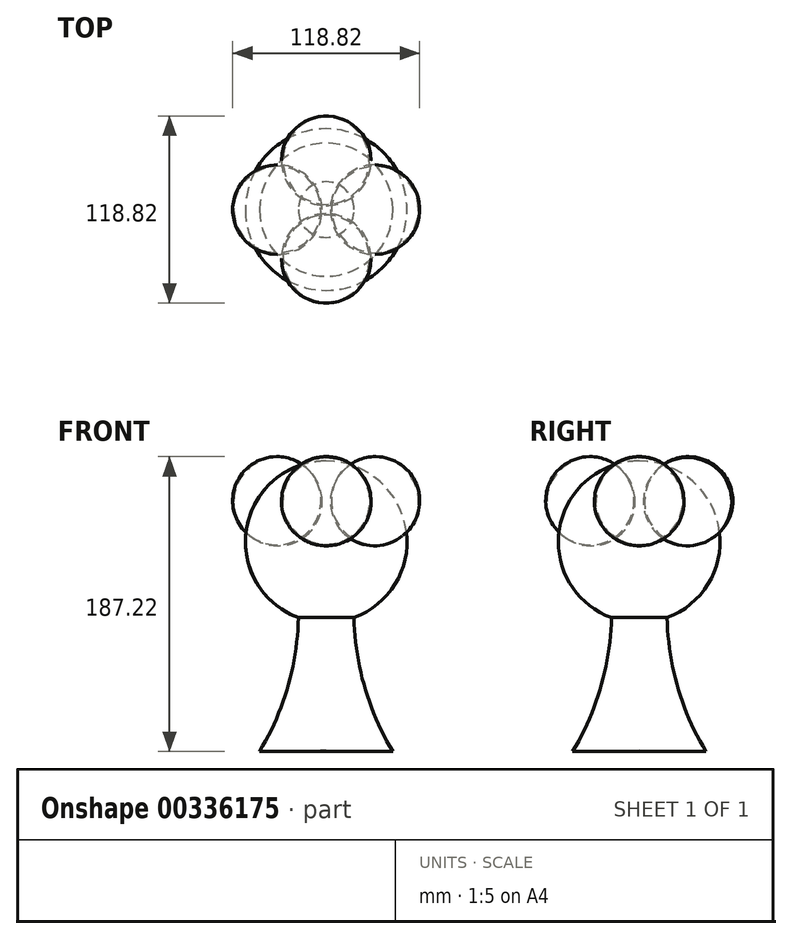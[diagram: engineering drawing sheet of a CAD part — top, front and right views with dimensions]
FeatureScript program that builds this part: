
annotation { "Feature Type Name" : "Feature", "Feature Type Description" : "" }
export const myFeature = defineFeature(function(context is Context, id is Id, definition is map)
    precondition{}
    {
        {
            var Q0;
            Q0=qCreatedBy(makeId("Front.planeOp"),FACE);
            var sketch = newSketch(context, id + "F0", { "sketchPlane" : qUnion([Q0])});
            skArc(sketch, "E0", {"start": v(-42.29, -76.52) * mm, "mid": v(-19.47, -12.95) * mm, "end": v(-22.96, 54.5) * mm});
            skLineSegment(sketch, "E1", {"start": v(-22.96, 54.5) * mm, "end": v(0, 54.5) * mm});
            skLineSegment(sketch, "E2", {"start": v(0, 54.5) * mm, "end": v(0, -75.98) * mm});
            skLineSegment(sketch, "E3", {"start": v(0, -75.98) * mm, "end": v(-42.29, -76.52) * mm});
            skSolve(sketch);
        }
        {
            var Q0;
            Q0=makeQuery(id+"F0.imprint","IMPRINT",FACE,{"disambiguationData":[TD([[makeQuery(id+"F0.imprint","IMPRINT",EDGE,{"derivedFrom":sQuery(id+"F0.wireOp",EDGE,"E0")}),-1.0]])]});
            var Q1;
            Q1=sQuery(id+"F0.wireOp",EDGE,"E2");
            revolve(context, id + "F1", {"entities" : qUnion([Q0]), "axis" : qUnion([Q1]), "revolveType" : RevolveType.FULL});
        }
        {
            var Q0;
            Q0=qCreatedBy(makeId("Front.planeOp"),FACE);
            var sketch = newSketch(context, id + "F2", { "sketchPlane" : qUnion([Q0])});
            skArc(sketch, "E4", {"start": v(0, 5.29) * mm, "mid": v(51.33, 56.61) * mm, "end": v(0, 107.94) * mm});
            skLineSegment(sketch, "E5", {"start": v(0, 5.29) * mm, "end": v(0, 107.94) * mm});
            skSolve(sketch);
        }
        {
            var Q0;
            Q0=makeQuery(id+"F2.imprint","IMPRINT",FACE,{"disambiguationData":[TD([[makeQuery(id+"F2.imprint","IMPRINT",EDGE,{"derivedFrom":sQuery(id+"F2.wireOp",EDGE,"E4")}),1.0]])]});
            var Q1;
            Q1=sQuery(id+"F2.wireOp",EDGE,"E5");
            revolve(context, id + "F3", {"operationType" : NewBodyOperationType.ADD, "entities" : qUnion([Q0]), "axis" : qUnion([Q1]), "revolveType" : RevolveType.FULL});
        }
        {
            var Q0;
            Q0=qCreatedBy(makeId("Right.planeOp"),FACE);
            var sketch = newSketch(context, id + "F4", { "sketchPlane" : qUnion([Q0])});
            skArc(sketch, "E6", {"start": v(48.3, 60.28) * mm, "mid": v(53.47, 99.92) * mm, "end": v(13.76, 104.5) * mm});
            skLineSegment(sketch, "E7", {"start": v(13.76, 104.5) * mm, "end": v(48.3, 60.28) * mm});
            skSolve(sketch);
        }
        {
            var Q0;
            Q0=makeQuery(id+"F4.imprint","IMPRINT",FACE,{"disambiguationData":[TD([[makeQuery(id+"F4.imprint","IMPRINT",EDGE,{"derivedFrom":sQuery(id+"F4.wireOp",EDGE,"E6")}),1.0]])]});
            var Q1;
            Q1=sQuery(id+"F4.wireOp",EDGE,"E7");
            revolve(context, id + "F5", {"entities" : qUnion([Q0]), "axis" : qUnion([Q1]), "revolveType" : RevolveType.FULL});
        }
        {
            var Q0;
            Q0=makeQuery(id+"F5.opRevolve","SWEPT_BODY",BODY,{"disambiguationData":[OSD([sQuery(id+"F4.wireOp",EDGE,"E6"),sQuery(id+"F4.wireOp",EDGE,"E7")])]});
            var Q1;
            Q1=makeQuery(id+"F1.opRevolve","SWEPT_EDGE",EDGE,{"disambiguationData":[OSD([sQuery(id+"F0.wireOp",EDGE,"E0"),sQuery(id+"F0.wireOp",EDGE,"E3")])]});
            circularPattern(context, id + "F6", {"entities" : qUnion([Q0]), "axis" : qUnion([Q1]), "angle" : 360 * degree, "instanceCount" : 4, "equalSpace" : true});
        }
    });
